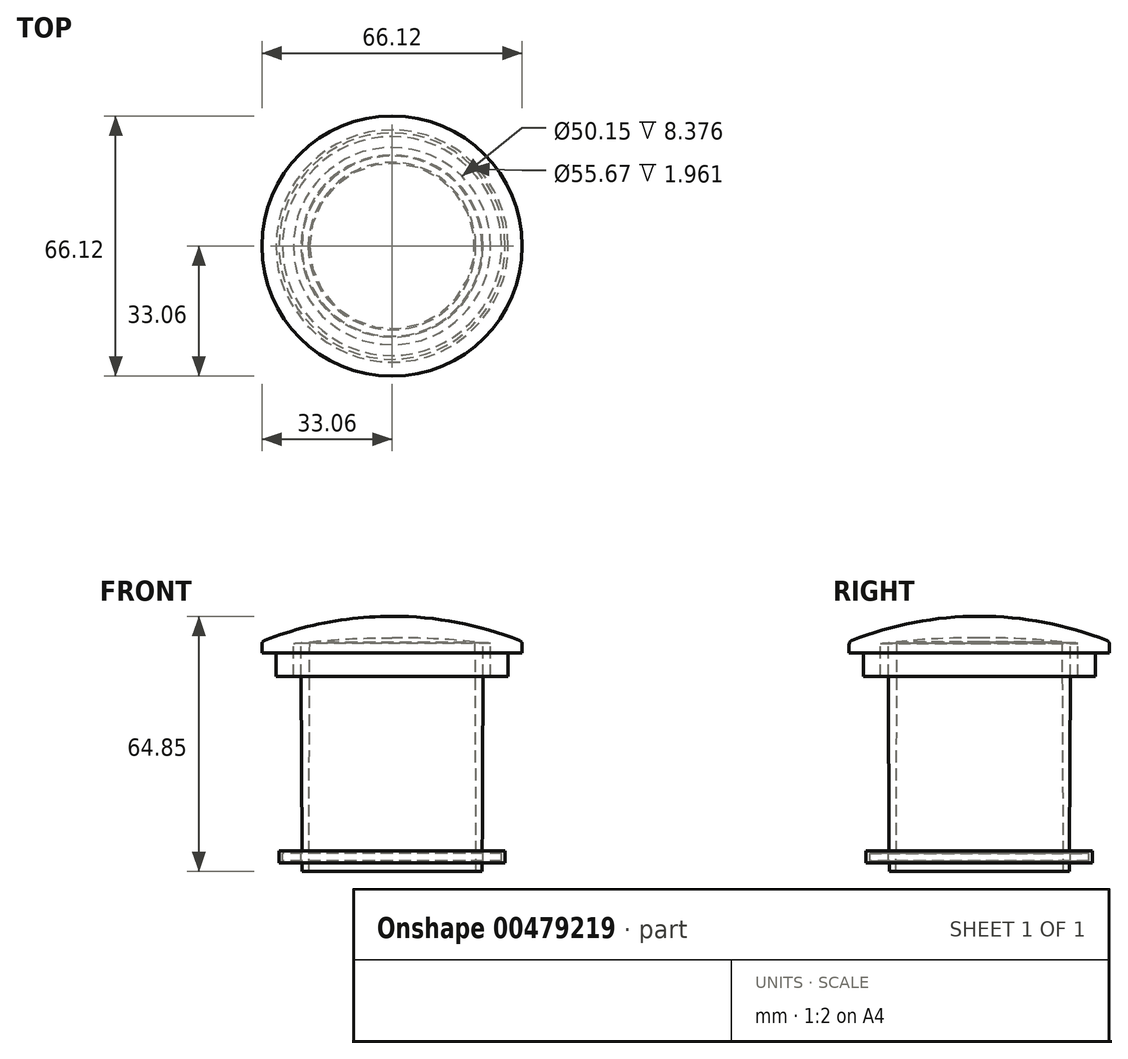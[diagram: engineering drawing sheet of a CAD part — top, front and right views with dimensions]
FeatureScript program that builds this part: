
annotation { "Feature Type Name" : "Feature", "Feature Type Description" : "" }
export const myFeature = defineFeature(function(context is Context, id is Id, definition is map)
    precondition{}
    {
        {
            var Q0;
            Q0=qCreatedBy(makeId("Front.planeOp"),FACE);
            var sketch = newSketch(context, id + "F0", { "sketchPlane" : qUnion([Q0])});
            skLineSegment(sketch, "E0", {"start": v(30.53, 20.83) * mm, "end": v(30.52, 20.83) * mm});
            skLineSegment(sketch, "E1", {"start": v(-30.52, 20.83) * mm, "end": v(-30.5, 20.83) * mm});
            skLineSegment(sketch, "E2", {"start": v(-21.27, -32.92) * mm, "end": v(-21, 25.43) * mm});
            skLineSegment(sketch, "E3", {"start": v(-22.89, -32.92) * mm, "end": v(-21.26, -32.92) * mm});
            skLineSegment(sketch, "E4", {"start": v(21.26, -32.92) * mm, "end": v(22.89, -32.92) * mm});
            skLineSegment(sketch, "E5", {"start": v(22.89, -32.92) * mm, "end": v(23.14, 25.22) * mm});
            skLineSegment(sketch, "E6", {"start": v(-22.89, -32.92) * mm, "end": v(-22.9, -30.7) * mm});
            skLineSegment(sketch, "E7", {"start": v(-33.06, 24.83) * mm, "end": v(-33.06, 22.67) * mm});
            skArc(sketch, "E8", {"start": v(-32.42, 25.77) * mm, "mid": v(-32.88, 25.4) * mm, "end": v(-33.06, 24.83) * mm});
            skArc(sketch, "E9", {"start": v(33.06, 24.83) * mm, "mid": v(32.88, 25.4) * mm, "end": v(32.42, 25.77) * mm});
            skLineSegment(sketch, "E10", {"start": v(29.5, 22.67) * mm, "end": v(33.06, 22.67) * mm});
            skLineSegment(sketch, "E11", {"start": v(33.06, 22.67) * mm, "end": v(33.06, 24.83) * mm});
            skLineSegment(sketch, "E12", {"start": v(29.5, 16.67) * mm, "end": v(29.5, 22.67) * mm});
            skLineSegment(sketch, "E13", {"start": v(25.08, 25.04) * mm, "end": v(25.08, 16.67) * mm});
            skLineSegment(sketch, "E14", {"start": v(25.08, 16.67) * mm, "end": v(29.5, 16.67) * mm});
            skLineSegment(sketch, "E15", {"start": v(-25.07, 16.67) * mm, "end": v(-25.07, 23.07) * mm});
            skLineSegment(sketch, "E16", {"start": v(-29.5, 22.67) * mm, "end": v(-29.5, 16.67) * mm});
            skLineSegment(sketch, "E17", {"start": v(-29.5, 16.67) * mm, "end": v(-25.07, 16.67) * mm});
            skLineSegment(sketch, "E18", {"start": v(-33.06, 22.67) * mm, "end": v(-29.5, 22.67) * mm});
            skLineSegment(sketch, "E19", {"start": v(-25.07, 16.67) * mm, "end": v(-25.07, 25.04) * mm});
            skArc(sketch, "E20", {"start": v(25.08, 25.04) * mm, "mid": v(24.1, 25.14) * mm, "end": v(23.14, 25.22) * mm});
            skArc(sketch, "E21", {"start": v(-23.14, 25.22) * mm, "mid": v(-24.1, 25.14) * mm, "end": v(-25.08, 25.04) * mm});
            skArc(sketch, "E22", {"start": v(21, 25.43) * mm, "mid": v(0, 26.48) * mm, "end": v(-21, 25.43) * mm});
            skLineSegment(sketch, "E23", {"start": v(21.26, -32.92) * mm, "end": v(21, 25.43) * mm});
            skArc(sketch, "E24", {"start": v(32.42, 25.77) * mm, "mid": v(0, 31.93) * mm, "end": v(-32.42, 25.77) * mm});
            skLineSegment(sketch, "E25", {"start": v(-21, 25.43) * mm, "end": v(21, 25.43) * mm});
            skLineSegment(sketch, "E26", {"start": v(0, 42.55) * mm, "end": v(0, -52.22) * mm});
            skLineSegment(sketch, "E27.bottom", {"start": v(-28.76, -27.63) * mm, "end": v(-22.91, -27.63) * mm});
            skLineSegment(sketch, "E27.top", {"start": v(-28.76, -30.7) * mm, "end": v(-22.9, -30.7) * mm});
            skLineSegment(sketch, "E27.left", {"start": v(-28.76, -27.63) * mm, "end": v(-28.76, -30.7) * mm});
            skLineSegment(sketch, "E28.trimOffspring", {"start": v(-22.91, -27.63) * mm, "end": v(-23.14, 25.22) * mm});
            skLineSegment(sketch, "E29.bottom", {"start": v(-27.83, -30.22) * mm, "end": v(-23.12, -30.22) * mm});
            skLineSegment(sketch, "E29.top", {"start": v(-27.83, -28.26) * mm, "end": v(-23.12, -28.26) * mm});
            skLineSegment(sketch, "E29.left", {"start": v(-27.83, -30.22) * mm, "end": v(-27.83, -28.26) * mm});
            skLineSegment(sketch, "E29.right", {"start": v(-23.12, -30.22) * mm, "end": v(-23.12, -28.26) * mm});
            skPoint(sketch, "E29.middle", {"position": v(-25.48, -29.24) * mm});
            skSolve(sketch);
        }
        {
            var Q0;
            {var subQ1=sQuery(id+"F0.wireOp",EDGE,"E2");Q0=makeQuery(id+"F0.imprint","IMPRINT",FACE,{"disambiguationData":[TD([[makeQuery(id+"F0.imprint","IMPRINT",EDGE,{"derivedFrom":subQ1}),1.0]])]});}
            var Q1;
            {var subQ5=sQuery(id+"F0.wireOp",EDGE,"E27.left");Q1=makeQuery(id+"F0.imprint","IMPRINT",FACE,{"disambiguationData":[TD([[makeQuery(id+"F0.imprint","IMPRINT",EDGE,{"derivedFrom":subQ5}),1.0]])]});}
            var Q2;
            Q2=sQuery(id+"F0.wireOp",EDGE,"E26");
            revolve(context, id + "F1", {"entities" : qUnion([Q0, Q1]), "axis" : qUnion([Q2]), "revolveType" : RevolveType.FULL});
        }
    });
